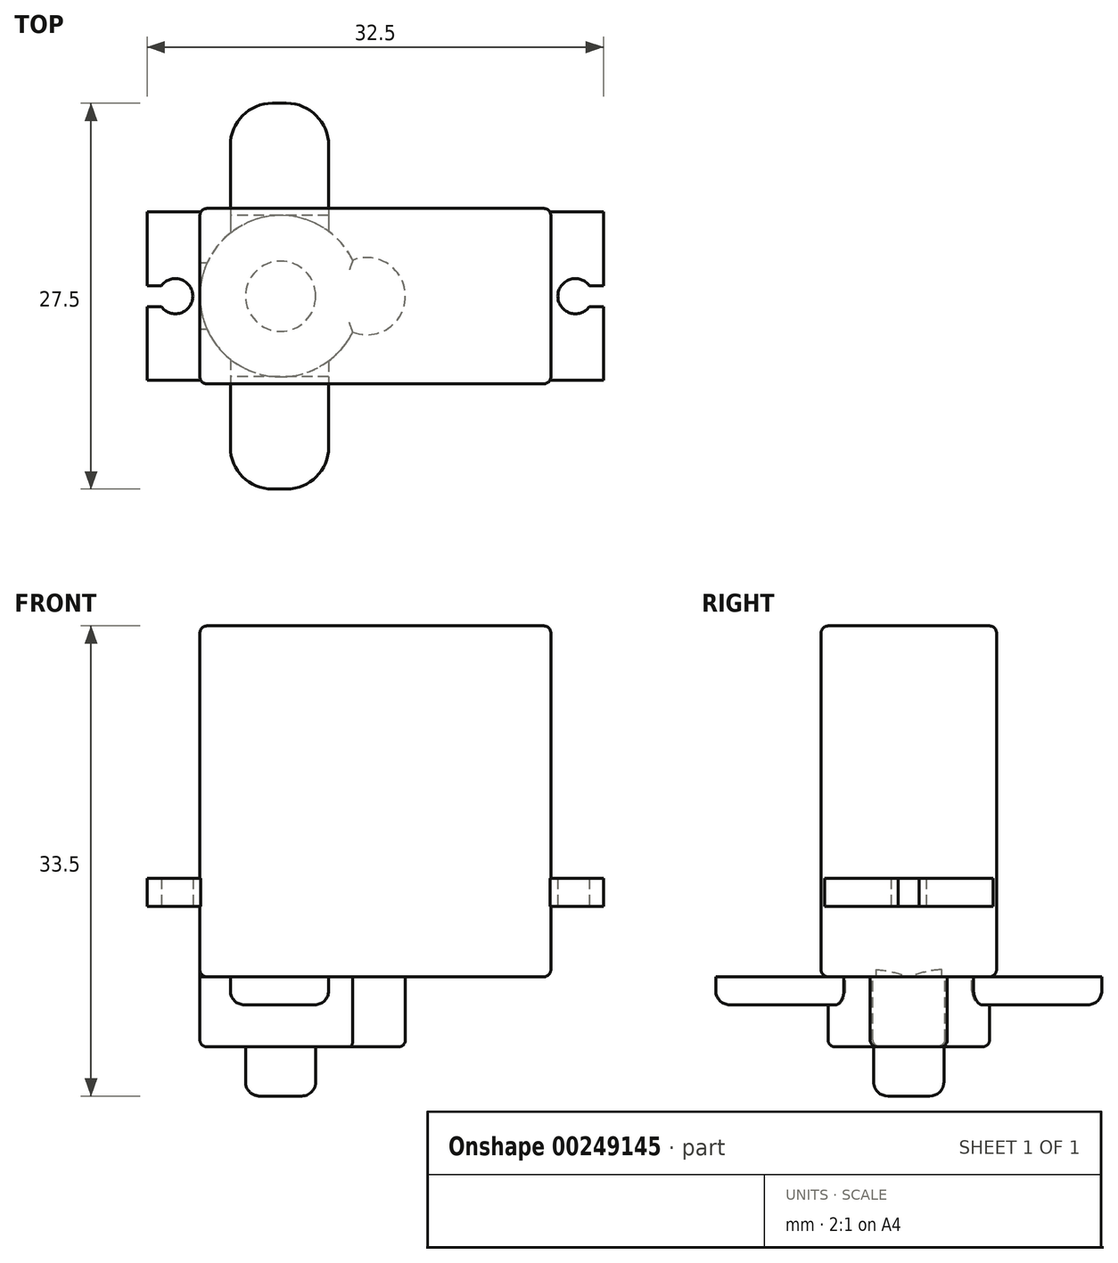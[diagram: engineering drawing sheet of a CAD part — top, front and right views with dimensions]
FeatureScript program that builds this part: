
annotation { "Feature Type Name" : "Feature", "Feature Type Description" : "" }
export const myFeature = defineFeature(function(context is Context, id is Id, definition is map)
    precondition{}
    {
        {
            var Q0;
            Q0=qCreatedBy(makeId("Top.planeOp"),FACE);
            var sketch = newSketch(context, id + "F0", { "sketchPlane" : qUnion([Q0])});
            skLineSegment(sketch, "E0.bottom", {"start": v(12.5, -6.25) * mm, "end": v(-12.5, -6.25) * mm});
            skLineSegment(sketch, "E0.top", {"start": v(12.5, 6.25) * mm, "end": v(-12.5, 6.25) * mm});
            skLineSegment(sketch, "E0.left", {"start": v(12.5, -6.25) * mm, "end": v(12.5, 6.25) * mm});
            skLineSegment(sketch, "E0.right", {"start": v(-12.5, -6.25) * mm, "end": v(-12.5, 6.25) * mm});
            skPoint(sketch, "E0.middle", {"position": v(0, 0) * mm});
            skSolve(sketch);
        }
        {
            var Q0;
            Q0 = qSketchRegion(id + "F0", true);
            extrude(context, id + "F1", {"entities" : qUnion([Q0]), "depth" : 25 * mm});
        }
        {
            var Q0;
            Q0=qCreatedBy(makeId("Top.planeOp"),FACE);
            var sketch = newSketch(context, id + "F2", { "sketchPlane" : qUnion([Q0])});
            skLineSegment(sketch, "E1.bottom", {"start": v(16.25, -6) * mm, "end": v(-16.25, -6) * mm});
            skLineSegment(sketch, "E1.top", {"start": v(16.25, 6) * mm, "end": v(-16.25, 6) * mm});
            skLineSegment(sketch, "E1.left", {"start": v(16.25, -6) * mm, "end": v(16.25, -0.75) * mm});
            skLineSegment(sketch, "E1.right", {"start": v(-16.25, -6) * mm, "end": v(-16.25, -0.75) * mm});
            skPoint(sketch, "E1.middle", {"position": v(0, 0) * mm});
            skLineSegment(sketch, "E2", {"start": v(-16.25, 6) * mm, "end": v(-16.25, 0.75) * mm});
            skArc(sketch, "E3", {"start": v(-15.25, -0.75) * mm, "mid": v(-13, 0) * mm, "end": v(-15.25, 0.75) * mm});
            skArc(sketch, "E4", {"start": v(15.25, 0.75) * mm, "mid": v(13, 0) * mm, "end": v(15.25, -0.75) * mm});
            skLineSegment(sketch, "E5.bottom", {"start": v(-16.25, -0.75) * mm, "end": v(-15.25, -0.75) * mm});
            skLineSegment(sketch, "E5.top", {"start": v(-16.25, 0.75) * mm, "end": v(-15.25, 0.75) * mm});
            skLineSegment(sketch, "E6.bottom", {"start": v(16.25, -0.75) * mm, "end": v(15.25, -0.75) * mm});
            skLineSegment(sketch, "E6.top", {"start": v(16.25, 0.75) * mm, "end": v(15.25, 0.75) * mm});
            skLineSegment(sketch, "E7.trimOffspring", {"start": v(16.25, 0.75) * mm, "end": v(16.25, 6) * mm});
            skLineSegment(sketch, "E8.trimOffspring", {"start": v(-16.25, 0.75) * mm, "end": v(-16.25, 6) * mm});
            skSolve(sketch);
        }
        {
            var Q0;
            Q0=makeQuery(id+"F2.imprint","IMPRINT",FACE,{"disambiguationData":[TD([[makeQuery(id+"F2.imprint","IMPRINT",EDGE,{"derivedFrom":sQuery(id+"F2.wireOp",EDGE,"E1.bottom")}),-1.0]])]});
            extrude(context, id + "F3", {"entities" : qUnion([Q0]), "operationType" : NewBodyOperationType.ADD, "depth" : 7 * mm, "hasSecondDirection" : true, "secondDirectionOppositeDirection" : false, "secondDirectionDepth" : 5 * mm});
        }
        {
            var Q0;
            Q0=makeQuery(id+"F0.imprint","IMPRINT",FACE,{"disambiguationData":[TD([[makeQuery(id+"F0.imprint","IMPRINT",EDGE,{"derivedFrom":sQuery(id+"F0.wireOp",EDGE,"E0.bottom")}),-1.0]])]});
            var sketch = newSketch(context, id + "F4", { "sketchPlane" : qUnion([Q0])});
            skCircle(sketch, "E9", {"center": v(-6.75, 0) * mm, "radius": 5.75 * mm});
            skLineSegment(sketch, "E10", {"start": v(-6.75, 0) * mm, "end": v(-12.5, 0) * mm, "construction": true});
            skSolve(sketch);
        }
        {
            var Q0;
            Q0=makeQuery(id+"F4.imprint","IMPRINT",FACE,{"disambiguationData":[TD([[makeQuery(id+"F4.imprint","IMPRINT",EDGE,{"derivedFrom":sQuery(id+"F4.wireOp",EDGE,"E9")}),1.0]])]});
            var Q1;
            Q1=sQuery(id+"F4.wireOp",EDGE,"E10");
            extrude(context, id + "F5", {"entities" : qUnion([Q0]), "operationType" : NewBodyOperationType.ADD, "surfaceEntities" : qUnion([Q1]), "oppositeDirection" : true, "depth" : 5 * mm});
        }
        {
            var Q0;
            Q0=makeQuery(id+"F5.opExtrude","CAP_FACE",FACE,{"disambiguationData":[OSD([sQuery(id+"F4.wireOp",EDGE,"E9")])],"isStart":false});
            var sketch = newSketch(context, id + "F6", { "sketchPlane" : qUnion([Q0])});
            skCircle(sketch, "E11", {"center": v(-6.75, 0) * mm, "radius": 2.5 * mm});
            skSolve(sketch);
        }
        {
            var Q0;
            Q0=makeQuery(id+"F6.imprint","IMPRINT",FACE,{"disambiguationData":[TD([[makeQuery(id+"F6.imprint","IMPRINT",EDGE,{"derivedFrom":sQuery(id+"F6.wireOp",EDGE,"E11")}),1.0]])]});
            var Q1;
            Q1=sQuery(id+"F6.wireOp",EDGE,"E11");
            extrude(context, id + "F7", {"entities" : qUnion([Q0]), "operationType" : NewBodyOperationType.ADD, "surfaceEntities" : qUnion([Q1]), "depth" : 3.5 * mm});
        }
        {
            var Q0;
            Q0=makeQuery(id+"F7.opExtrude","CAP_EDGE",EDGE,{"disambiguationData":[OSD([sQuery(id+"F6.wireOp",EDGE,"E11")])],"isStart":false});
            fillet(context, id + "F8", {"entities" : qUnion([Q0]), "radius" : 1 * mm, "tangentPropagation" : true, "allowEdgeOverflow" : false});
        }
        {
            var Q0;
            Q0=makeQuery(id+"F2.imprint","IMPRINT",FACE,{"disambiguationData":[TD([[makeQuery(id+"F2.imprint","IMPRINT",EDGE,{"derivedFrom":sQuery(id+"F2.wireOp",EDGE,"E1.bottom")}),-1.0]])]});
            var sketch = newSketch(context, id + "F9", { "sketchPlane" : qUnion([Q0])});
            skLineSegment(sketch, "E12", {"start": v(-6.76, 0) * mm, "end": v(-0.6, 0) * mm});
            skCircle(sketch, "E13", {"center": v(-0.6, 0) * mm, "radius": 2.75 * mm});
            skSolve(sketch);
        }
        {
            var Q0;
            Q0=makeQuery(id+"F9.imprint","IMPRINT",FACE,{"disambiguationData":[TD([[makeQuery(id+"F9.imprint","IMPRINT",EDGE,{"derivedFrom":sQuery(id+"F9.wireOp",EDGE,"E13")}),1.0]])]});
            var Q1;
            Q1=sQuery(id+"F9.wireOp",EDGE,"E13");
            extrude(context, id + "F10", {"entities" : qUnion([Q0]), "operationType" : NewBodyOperationType.ADD, "surfaceEntities" : qUnion([Q1]), "oppositeDirection" : true, "depth" : 5 * mm});
        }
        {
            var Q0;
            Q0=makeQuery(id+"F5.opExtrude","CAP_EDGE",EDGE,{"disambiguationData":[OSD([sQuery(id+"F4.wireOp",EDGE,"E9")])],"isStart":false});
            var Q1;
            Q1=makeQuery(id+"F1.opExtrude","CAP_EDGE",EDGE,{"disambiguationData":[OSD([sQuery(id+"F0.wireOp",EDGE,"E0.top")])],"isStart":true});
            var Q2;
            Q2=makeQuery(id+"F1.opExtrude","CAP_EDGE",EDGE,{"disambiguationData":[OSD([sQuery(id+"F0.wireOp",EDGE,"E0.left")])],"isStart":true});
            var Q3;
            Q3=makeQuery(id+"F1.opExtrude","SWEPT_EDGE",EDGE,{"disambiguationData":[OSD([sQuery(id+"F0.wireOp",EDGE,"E0.top"),sQuery(id+"F0.wireOp",EDGE,"E0.left")])]});
            var Q4;
            Q4=makeQuery(id+"F1.opExtrude","SWEPT_EDGE",EDGE,{"disambiguationData":[OSD([sQuery(id+"F0.wireOp",EDGE,"E0.top"),sQuery(id+"F0.wireOp",EDGE,"E0.right")])]});
            var Q5;
            {var subQ0=sQuery(id+"F0.wireOp",EDGE,"E0.bottom");var subQ1=sQuery(id+"F0.wireOp",EDGE,"E0.right");Q5=makeQuery(id+"F5.boolean.opBoolean","SPLIT",EDGE,{"disambiguationData":[TD([makeQuery(id+"F1.opExtrude","SWEPT_FACE",FACE,{"disambiguationData":[OSD([subQ0])]})])],"derivedFrom":makeQuery(id+"F1.opExtrude","CAP_EDGE",EDGE,{"disambiguationData":[OSD([subQ1])],"isStart":true})});}
            var Q6;
            {var subQ0=sQuery(id+"F0.wireOp",EDGE,"E0.right");var subQ1=sQuery(id+"F0.wireOp",EDGE,"E0.top");Q6=makeQuery(id+"F5.boolean.opBoolean","SPLIT",EDGE,{"disambiguationData":[TD([makeQuery(id+"F1.opExtrude","SWEPT_FACE",FACE,{"disambiguationData":[OSD([subQ1])]})])],"derivedFrom":makeQuery(id+"F1.opExtrude","CAP_EDGE",EDGE,{"disambiguationData":[OSD([subQ0])],"isStart":true})});}
            var Q7;
            Q7=makeQuery(id+"F1.opExtrude","SWEPT_EDGE",EDGE,{"disambiguationData":[OSD([sQuery(id+"F0.wireOp",EDGE,"E0.bottom"),sQuery(id+"F0.wireOp",EDGE,"E0.right")])]});
            var Q8;
            Q8=makeQuery(id+"F1.opExtrude","SWEPT_EDGE",EDGE,{"disambiguationData":[OSD([sQuery(id+"F0.wireOp",EDGE,"E0.bottom"),sQuery(id+"F0.wireOp",EDGE,"E0.left")])]});
            var Q9;
            Q9=makeQuery(id+"F1.opExtrude","CAP_EDGE",EDGE,{"disambiguationData":[OSD([sQuery(id+"F0.wireOp",EDGE,"E0.bottom")])],"isStart":true});
            var Q10;
            Q10=makeQuery(id+"F1.opExtrude","CAP_EDGE",EDGE,{"disambiguationData":[OSD([sQuery(id+"F0.wireOp",EDGE,"E0.bottom")])],"isStart":false});
            var Q11;
            Q11=makeQuery(id+"F1.opExtrude","CAP_EDGE",EDGE,{"disambiguationData":[OSD([sQuery(id+"F0.wireOp",EDGE,"E0.left")])],"isStart":false});
            var Q12;
            Q12=makeQuery(id+"F1.opExtrude","CAP_EDGE",EDGE,{"disambiguationData":[OSD([sQuery(id+"F0.wireOp",EDGE,"E0.right")])],"isStart":false});
            var Q13;
            Q13=makeQuery(id+"F1.opExtrude","CAP_EDGE",EDGE,{"disambiguationData":[OSD([sQuery(id+"F0.wireOp",EDGE,"E0.top")])],"isStart":false});
            var Q14;
            Q14=makeQuery(id+"F10.opExtrude","CAP_EDGE",EDGE,{"disambiguationData":[OSD([sQuery(id+"F9.wireOp",EDGE,"E13")])],"isStart":false});
            fillet(context, id + "F11", {"entities" : qUnion([Q0, Q1, Q2, Q3, Q4, Q5, Q6, Q7, Q8, Q9, Q10, Q11, Q12, Q13, Q14]), "radius" : .5 * mm, "tangentPropagation" : true, "allowEdgeOverflow" : false});
        }
        {
            var Q0;
            Q0=qCreatedBy(makeId("Top.planeOp"),FACE);
            var sketch = newSketch(context, id + "F12", { "sketchPlane" : qUnion([Q0])});
            skCircle(sketch, "E14", {"center": v(-6.83, 0) * mm, "radius": 3.6 * mm});
            skLineSegment(sketch, "E15.bottom", {"start": v(-6.33, 13.75) * mm, "end": v(-7.33, 13.75) * mm});
            skLineSegment(sketch, "E15.top", {"start": v(-6.33, -13.75) * mm, "end": v(-7.33, -13.75) * mm});
            skLineSegment(sketch, "E15.left", {"start": v(-3.33, 10.75) * mm, "end": v(-3.33, -10.75) * mm});
            skLineSegment(sketch, "E15.right", {"start": v(-10.33, 10.75) * mm, "end": v(-10.33, -10.75) * mm});
            skLineSegment(sketch, "E16", {"start": v(0, 0) * mm, "end": v(-13.07, 0) * mm});
            skPoint(sketch, "E16.endSnap0", {"position": v(-8.95, 0) * mm});
            skPoint(sketch, "E17", {"position": v(-3.33, 0) * mm});
            skPoint(sketch, "E18", {"position": v(-4.72, 0) * mm});
            skPoint(sketch, "E19", {"position": v(-10.33, 0) * mm});
            skPoint(sketch, "E20.visualSharp", {"position": v(-10.33, -13.75) * mm});
            skArc(sketch, "E20.filletArc", {"start": v(-10.33, -10.75) * mm, "mid": v(-9.45, -12.87) * mm, "end": v(-7.33, -13.75) * mm});
            skPoint(sketch, "E21.visualSharp", {"position": v(-3.33, -13.75) * mm});
            skArc(sketch, "E21.filletArc", {"start": v(-6.33, -13.75) * mm, "mid": v(-4.21, -12.87) * mm, "end": v(-3.33, -10.75) * mm});
            skPoint(sketch, "E22.visualSharp", {"position": v(-3.33, 13.75) * mm});
            skArc(sketch, "E22.filletArc", {"start": v(-3.33, 10.75) * mm, "mid": v(-4.21, 12.87) * mm, "end": v(-6.33, 13.75) * mm});
            skPoint(sketch, "E23.visualSharp", {"position": v(-10.33, 13.75) * mm});
            skArc(sketch, "E23.filletArc", {"start": v(-7.33, 13.75) * mm, "mid": v(-9.45, 12.87) * mm, "end": v(-10.33, 10.75) * mm});
            skSolve(sketch);
        }
        {
            var Q0;
            {var subQ0=sQuery(id+"F12.wireOp",EDGE,"E15.right");var subQ1=sQuery(id+"F12.wireOp",EDGE,"E14");var subQ2=makeQuery(id+"F12.imprint","INTERSECT",VERTEX,{"disambiguationData":[OD(1.0)],"derivedFrom":[subQ1,subQ0]});Q0=makeQuery(id+"F12.imprint","IMPRINT",FACE,{"disambiguationData":[TD([[makeQuery(id+"F12.imprint","IMPRINT",EDGE,{"disambiguationData":[TD([[subQ2,-1.0]])],"derivedFrom":subQ1}),1.0]])]});}
            var Q1;
            {var subQ0=sQuery(id+"F12.wireOp",EDGE,"E15.left");var subQ1=sQuery(id+"F12.wireOp",EDGE,"E14");var subQ2=makeQuery(id+"F12.imprint","INTERSECT",VERTEX,{"disambiguationData":[OD(0.0)],"derivedFrom":[subQ1,subQ0]});Q1=makeQuery(id+"F12.imprint","IMPRINT",FACE,{"disambiguationData":[TD([[makeQuery(id+"F12.imprint","IMPRINT",EDGE,{"disambiguationData":[TD([[subQ2,-1.0]])],"derivedFrom":subQ1}),1.0]])]});}
            var Q2;
            Q2=sQuery(id+"F12.wireOp",EDGE,"E14");
            extrude(context, id + "F13", {"entities" : qUnion([Q0, Q1]), "surfaceEntities" : qUnion([Q2]), "oppositeDirection" : true, "depth" : 5 * mm});
        }
        {
            var Q0;
            Q0=makeQuery(id+"F12.imprint","IMPRINT",FACE,{"disambiguationData":[TD([[makeQuery(id+"F12.imprint","IMPRINT",EDGE,{"derivedFrom":sQuery(id+"F12.wireOp",EDGE,"E15.top")}),-1.0]])]});
            var Q1;
            Q1=makeQuery(id+"F12.imprint","IMPRINT",FACE,{"disambiguationData":[TD([[makeQuery(id+"F12.imprint","IMPRINT",EDGE,{"derivedFrom":sQuery(id+"F12.wireOp",EDGE,"E15.bottom")}),1.0]])]});
            extrude(context, id + "F14", {"entities" : qUnion([Q0, Q1]), "operationType" : NewBodyOperationType.ADD, "oppositeDirection" : true, "depth" : 2 * mm});
        }
        {
            var Q0;
            {var subQ0=sQuery(id+"F12.wireOp",EDGE,"E15.right");Q0=makeQuery(id+"F14.opExtrude","CAP_EDGE",EDGE,{"disambiguationData":[OSD([subQ0]),TDD([makeQuery(id+"F12.imprint","IMPRINT",EDGE,{"disambiguationData":[TD([[makeQuery(id+"F12.imprint","INTERSECT",VERTEX,{"derivedFrom":[subQ0,sQuery(id+"F12.wireOp",EDGE,"E20.filletArc")]}),1.0]])],"derivedFrom":subQ0})])],"isStart":false});}
            var Q1;
            Q1=makeQuery(id+"F14.opExtrude","CAP_EDGE",EDGE,{"disambiguationData":[OSD([sQuery(id+"F12.wireOp",EDGE,"E20.filletArc")])],"isStart":false});
            var Q2;
            Q2=makeQuery(id+"F14.opExtrude","CAP_EDGE",EDGE,{"disambiguationData":[OSD([sQuery(id+"F12.wireOp",EDGE,"E21.filletArc")])],"isStart":false});
            var Q3;
            {var subQ0=sQuery(id+"F12.wireOp",EDGE,"E15.left");Q3=makeQuery(id+"F14.opExtrude","CAP_EDGE",EDGE,{"disambiguationData":[OSD([subQ0]),TDD([makeQuery(id+"F12.imprint","IMPRINT",EDGE,{"disambiguationData":[TD([[makeQuery(id+"F12.imprint","INTERSECT",VERTEX,{"derivedFrom":[subQ0,sQuery(id+"F12.wireOp",EDGE,"E21.filletArc")]}),1.0]])],"derivedFrom":subQ0})])],"isStart":false});}
            var Q4;
            {var subQ0=sQuery(id+"F12.wireOp",EDGE,"E15.right");Q4=makeQuery(id+"F14.opExtrude","CAP_EDGE",EDGE,{"disambiguationData":[OSD([subQ0]),TDD([makeQuery(id+"F12.imprint","IMPRINT",EDGE,{"disambiguationData":[TD([[makeQuery(id+"F12.imprint","INTERSECT",VERTEX,{"derivedFrom":[subQ0,sQuery(id+"F12.wireOp",EDGE,"E23.filletArc")]}),-1.0]])],"derivedFrom":subQ0})])],"isStart":false});}
            var Q5;
            Q5=makeQuery(id+"F14.opExtrude","CAP_EDGE",EDGE,{"disambiguationData":[OSD([sQuery(id+"F12.wireOp",EDGE,"E23.filletArc")])],"isStart":false});
            var Q6;
            Q6=makeQuery(id+"F14.opExtrude","CAP_EDGE",EDGE,{"disambiguationData":[OSD([sQuery(id+"F12.wireOp",EDGE,"E22.filletArc")])],"isStart":false});
            fillet(context, id + "F15", {"entities" : qUnion([Q0, Q1, Q2, Q3, Q4, Q5, Q6]), "radius" : 1 * mm, "tangentPropagation" : true, "allowEdgeOverflow" : false});
        }
    });
